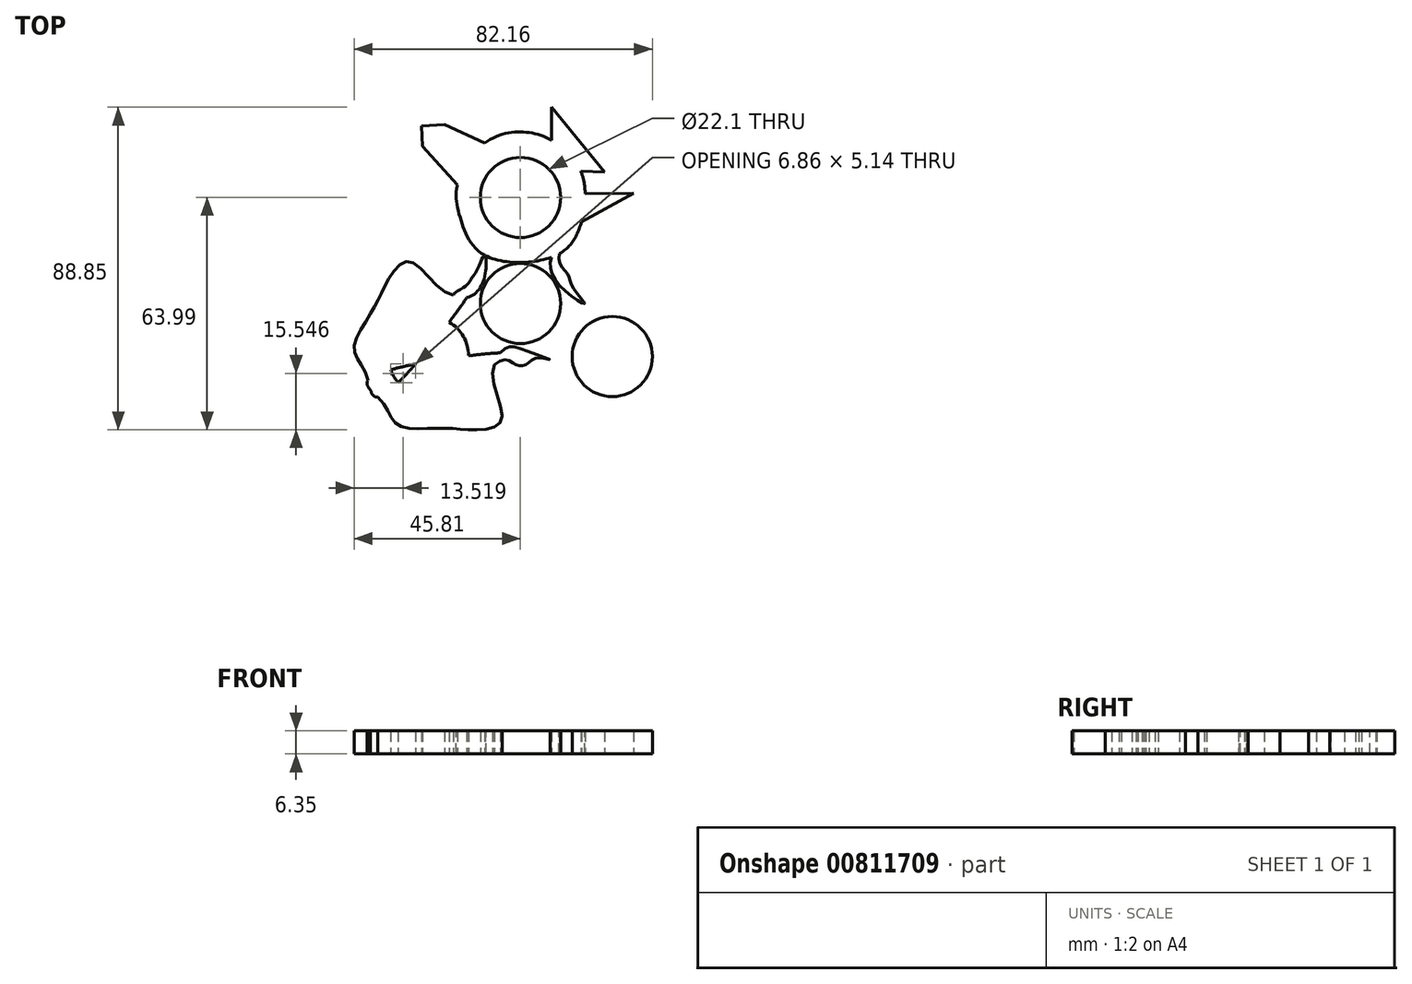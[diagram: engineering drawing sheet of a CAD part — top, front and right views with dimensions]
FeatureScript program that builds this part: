
annotation { "Feature Type Name" : "Feature", "Feature Type Description" : "" }
export const myFeature = defineFeature(function(context is Context, id is Id, definition is map)
    precondition{}
    {
        {
            var Q0;
            Q0=qCreatedBy(makeId("Top.planeOp"),FACE);
            var sketch = newSketch(context, id + "F0", { "sketchPlane" : qUnion([Q0])});
            skCircle(sketch, "E0", {"center": v(0, 0) * mm, "radius": 11.05 * mm});
            skCircle(sketch, "E1", {"center": v(0, 29.21) * mm, "radius": 11.05 * mm});
            skCircle(sketch, "E2", {"center": v(25.3, -14.6) * mm, "radius": 11.05 * mm});
            skCircle(sketch, "E3", {"center": v(-25.3, -14.6) * mm, "radius": 11.05 * mm});
            skFitSpline(sketch, "E4.trimOffspring", {"points": [v(-41.81, -20.94) * mm, v(-38.27, -26.89) * mm, v(-33.68, -33.45) * mm, v(-22.47, -34.33) * mm, v(-13.51, -34.76) * mm, v(-5.22, -32.01) * mm, v(-7.26, -17.16) * mm, v(-3.2, -13.69) * mm, v(-41.81, -20.94) * mm]});
            skFitSpline(sketch, "E5.trimOffspring", {"points": [v(-39.04, -25.74) * mm, v(-42.42, -19.7) * mm, v(-45.8, -12.45) * mm, v(-40.97, -2.3) * mm, v(-36.86, 5.68) * mm, v(-30.34, 11.48) * mm, v(-18.5, 2.3) * mm, v(-13.45, 4.07) * mm, v(-39.04, -25.74) * mm]});
            skLineSegment(sketch, "E6.MirrorC", {"start": v(-10.4, 9.46) * mm, "end": v(-10.4, 9.46) * mm});
            skFitSpline(sketch, "E7", {"points": [v(-9.88, 13.3) * mm, v(-16.37, 22.95) * mm, v(-17.4, 32.6) * mm, v(-9.88, 44.18) * mm, v(0, 47.28) * mm, v(8.53, 44.98) * mm, v(16.67, 36.38) * mm, v(16.79, 22.5) * mm, v(9.88, 13.3) * mm, v(-9.88, 13.3) * mm]});
            skLineSegment(sketch, "E8", {"start": v(-17.4, 32.6) * mm, "end": v(-27.04, 43.38) * mm});
            skLineSegment(sketch, "E9", {"start": v(-27.04, 43.38) * mm, "end": v(-27.27, 48.88) * mm});
            skLineSegment(sketch, "E10", {"start": v(-27.27, 48.88) * mm, "end": v(-20.96, 49.23) * mm});
            skLineSegment(sketch, "E11", {"start": v(-20.96, 49.23) * mm, "end": v(-9.87, 44.19) * mm});
            skLineSegment(sketch, "E12", {"start": v(8.53, 44.98) * mm, "end": v(8.53, 54.07) * mm});
            skLineSegment(sketch, "E13", {"start": v(8.53, 54.07) * mm, "end": v(23.12, 36.21) * mm});
            skLineSegment(sketch, "E14", {"start": v(23.12, 36.21) * mm, "end": v(16.64, 36.46) * mm});
            skLineSegment(sketch, "E15", {"start": v(16.79, 22.5) * mm, "end": v(31.21, 30.42) * mm});
            skLineSegment(sketch, "E16", {"start": v(31.21, 30.42) * mm, "end": v(17.8, 30.28) * mm});
            skFitSpline(sketch, "E17", {"points": [v(-18.5, 2.3) * mm, v(-14.83, 5.02) * mm, v(-13.54, 6.82) * mm, v(-11.95, 9.2) * mm, v(-9.88, 13.3) * mm, v(-9.88, 7.18) * mm, v(-14.73, 1.67) * mm, v(-18.5, 2.3) * mm]});
            skFitSpline(sketch, "E18.trimOffspring", {"points": [v(-9.88, 13.3) * mm, v(-16.37, 22.95) * mm, v(-17.4, 32.6) * mm, v(-9.88, 44.18) * mm, v(0, 47.28) * mm, v(8.53, 44.98) * mm, v(16.67, 36.38) * mm, v(16.79, 22.5) * mm, v(9.88, 13.3) * mm, v(-9.88, 13.3) * mm]});
            skFitSpline(sketch, "E19", {"points": [v(10.87, 15.53) * mm, v(10.66, 11.61) * mm, v(13.08, 7.96) * mm, v(14.42, 4.45) * mm, v(17.67, 0) * mm, v(10.82, 4.92) * mm, v(8.6, 12.8) * mm, v(10.87, 15.53) * mm]});
            skFitSpline(sketch, "E20.trimOffspring", {"points": [v(13.76, 2.86) * mm, v(19.6, 0.37) * mm, v(25.5, 3.2) * mm, v(22.64, 10.6) * mm, v(24.74, 12.05) * mm, v(29.5, 4.2) * mm, v(31.63, 4.61) * mm, v(27.77, 13.32) * mm, v(30.14, 14.93) * mm, v(35.62, 4.21) * mm, v(40.28, -1.21) * mm, v(49.96, 5.66) * mm, v(52.6, 2.72) * mm, v(42.1, -6.4) * mm, v(42.33, -9.44) * mm, v(53.46, -3.25) * mm, v(55.64, -5.4) * mm, v(43.78, -12.37) * mm, v(41.02, -20.43) * mm, v(37.35, -21.66) * mm, v(37.35, -21.66) * mm, v(13.76, 2.86) * mm]});
            skFitSpline(sketch, "E21", {"points": [v(-9.01, -18.47) * mm, v(-5.2, -15.68) * mm, v(-1.96, -16.4) * mm, v(0, -17.18) * mm, v(2.11, -16.46) * mm, v(4.69, -14.96) * mm, v(8.14, -15.48) * mm, v(0, -12.5) * mm, v(-4.69, -12.75) * mm, v(-9.01, -18.47) * mm]});
            skFitSpline(sketch, "E22.trimOffspring", {"points": [v(4.4, -13.35) * mm, v(9.48, -17.16) * mm, v(9.99, -23.68) * mm, v(2.14, -24.9) * mm, v(1.94, -27.45) * mm, v(11.1, -27.66) * mm, v(11.82, -29.7) * mm, v(2.35, -30.71) * mm, v(2.14, -33.56) * mm, v(14.16, -32.95) * mm, v(21.2, -34.28) * mm, v(20.07, -46.1) * mm, v(23.94, -46.91) * mm, v(26.6, -33.26) * mm, v(29.34, -31.93) * mm, v(29.55, -44.67) * mm, v(32.5, -45.48) * mm, v(32.6, -31.73) * mm, v(38.2, -25.31) * mm, v(37.44, -21.51) * mm, v(37.44, -21.51) * mm, v(4.4, -13.35) * mm]});
            skSolve(sketch);
        }
        {
            var Q0;
            Q0 = qSketchRegion(id + "F0", true);
            extrude(context, id + "F1", {"entities" : qUnion([Q0]), "depth" : 6.35 * mm, "offsetDistance" : 25.4 * mm});
        }
    });
